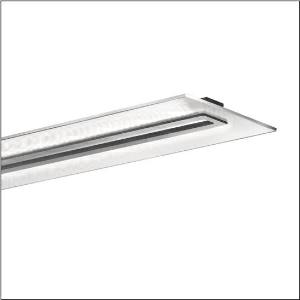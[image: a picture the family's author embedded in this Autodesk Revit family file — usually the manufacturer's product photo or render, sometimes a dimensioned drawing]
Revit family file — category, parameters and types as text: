
# Revit family: vega_r__11_5mn238dlc0s_c747
name_source: partatom
category: Lighting Fixtures
units: mm (PartAtom-declared; Revit-internal decimal feet)

## family parameters
Cut with Voids When Loaded = No
Host = Face
Light Source = No
Part Type = Normal
Room Calculation Point = No
Round Connector Dimension = Use Diameter
Shared = No

## types (1)
- --- (1 x LED 4000K / CRI = 80 (unbekannt), 4300 lm, 4000K)
    Apparent Load = 31 VA
    CIE Flux Codes = 61 86 97 62 100
    Color Rendering = 80
    Color Temperature = 4000K
    Default Elevation = 1800 mm
    Description = Vega® 11, office luminaire, primary light control with prismatic reflector, of PMMA, transparent prismatic structure, CAT 2 (L<= 1500cd/m²), light emission: direct/indirect distribution, primary light characteristic: symmetric, installation type: suspended mounting, surface-mounted, LED, rated luminous flux: 4.300lm, luminous efficacy: 139lm/W, light colour: 840, colour temperature: 4000K, control gear: ECG, with terminal, 3+2-pole, max. 2.5mm², mains connection: 230V, AC, 50Hz, connection cable inclusive, cable length: 1,5m, rated input power: 31W, luminaire housing, rectangular, rounded, of aluminium section, anodised, metallic grey (RAL 9006), length: 1.250mm, width: 350mm, height: 43mm, luminaire housing, lower part, of aluminium section, anodised, metallic grey (RAL 9006), of PC, grey, protection rating (complete): IP20, insulation class (complete): insulation class I (protective earthing), certification: CE, permissible operating ambient temperature: 0..+35°C, standard: EN 50419, packaging unit: 1 piece
    Height = 40 mm  [stored 0.131234 ft]
    Lamp = 1 x LED 4000K / CRI >= 80 (unbekannt)
    Lamp Light Flux = 4300 lm
    Lamp count = 1
    Length = 1250 mm
    Luminous efficacy = 139 lm/W
    Manufacturer = Siteco
    ModVariant = No
    Model = 5MN238DLC0S
    Mounting Place = Ceiling
    Mounting Type = Pendant
    Number of Poles = 1
    OnlyDefault = Yes
    Power Factor = 1
    Product Name = Vega® 11
    Product group = office luminaire | ceiling pendant
    ProductGroupID = 902
    Protection Class = Protection class I
    Protection Degree = IP 20
    RLX_Detail_Level = 1
    RLX_Emergency_Light_Flux = 0 lm
    RLX_Emergency_Type = 0
    RLX_Emergency_Type_DB = No
    RlxData = <blob elided: 62997 chars, md5=925256c7>
    Socket = socket
    Standby Power = 0 W
    System Light Flux = 4300 lm
    System Power = 31 W
    Type Comments = factory setting: luminous flux: 100 % | dim-lin: 254 | 231 mA
    Type Image = l_1004807.jpg
    URL = http://relux.com
    VarID = @adj_149917
    Voltage = 0 V
    Weight = 0.00 kg
    Width = 350 mm

note: [stored X ft] marks values corroborated as IEEE doubles in the binary element streams (Revit-internal decimal feet)

## geometry (parser evidence)
native form markers: Blend x4, Sweep x13
no freeform markers — native parametric forms only
